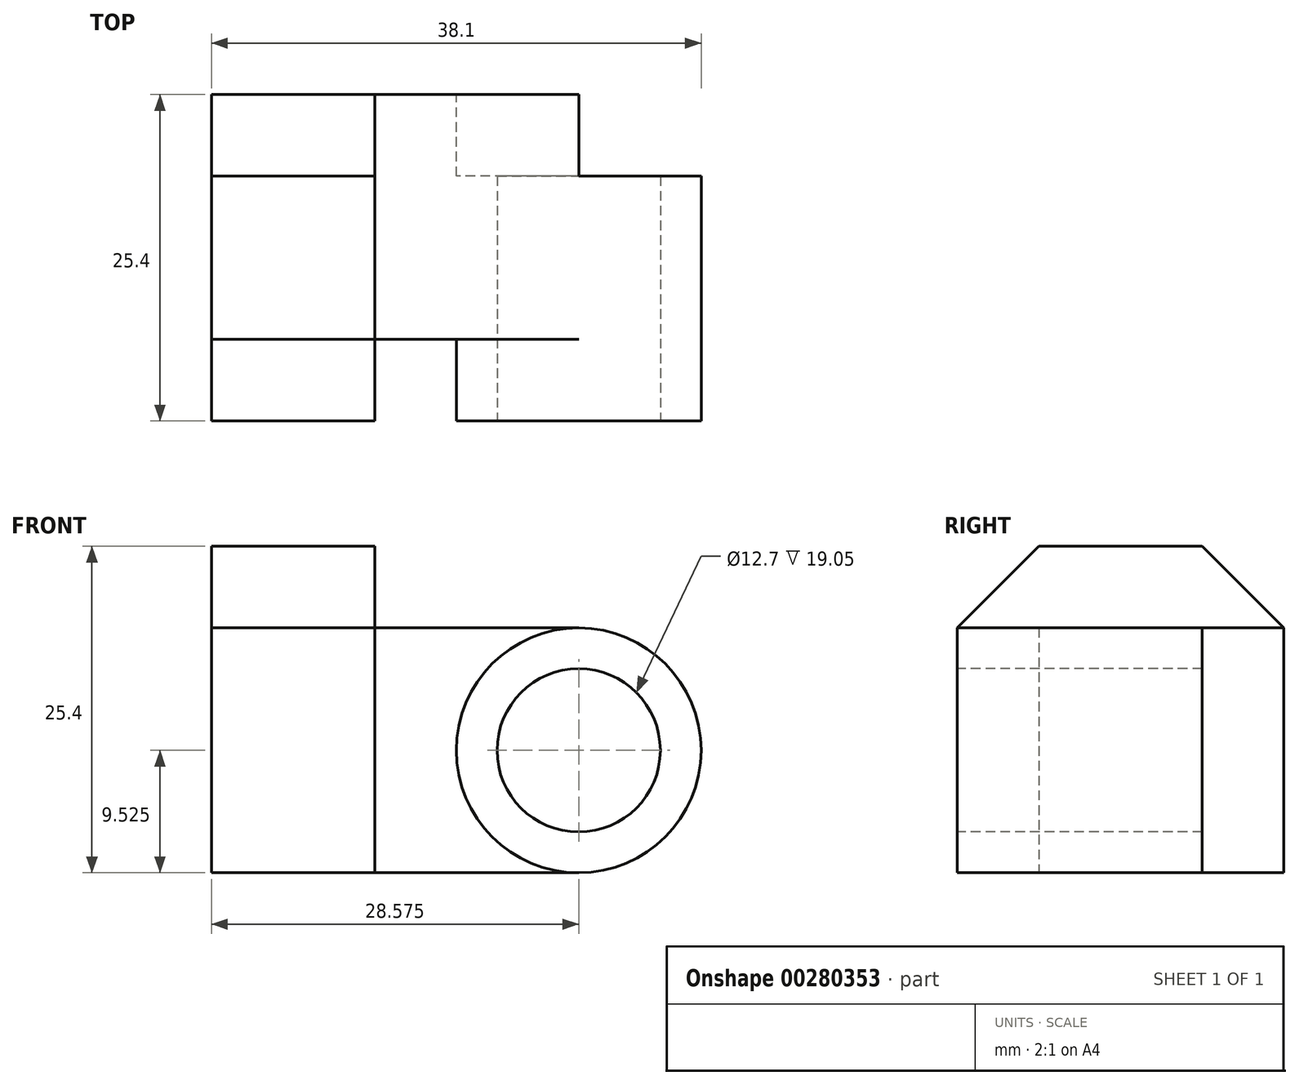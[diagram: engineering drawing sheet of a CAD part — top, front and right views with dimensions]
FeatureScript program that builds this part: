
annotation { "Feature Type Name" : "Feature", "Feature Type Description" : "" }
export const myFeature = defineFeature(function(context is Context, id is Id, definition is map)
    precondition{}
    {
        {
            var Q0;
            Q0=qCreatedBy(makeId("Top.planeOp"),FACE);
            var sketch = newSketch(context, id + "F0", { "sketchPlane" : qUnion([Q0])});
            skLineSegment(sketch, "E0.bottom", {"start": v(0, 0) * mm, "end": v(38.1, 0) * mm});
            skLineSegment(sketch, "E0.top", {"start": v(0, 25.4) * mm, "end": v(38.1, 25.4) * mm});
            skLineSegment(sketch, "E0.left", {"start": v(0, 0) * mm, "end": v(0, 25.4) * mm});
            skLineSegment(sketch, "E0.right", {"start": v(38.1, 0) * mm, "end": v(38.1, 25.4) * mm});
            skSolve(sketch);
        }
        {
            var Q0;
            Q0 = qSketchRegion(id + "F0", true);
            extrude(context, id + "F1", {"entities" : qUnion([Q0]), "depth" : 25.4 * mm});
        }
        {
            var Q0;
            Q0=makeQuery(id+"F1.opExtrude","SWEPT_FACE",FACE,{"disambiguationData":[OSD([sQuery(id+"F0.wireOp",EDGE,"E0.left")])]});
            var sketch = newSketch(context, id + "F2", { "sketchPlane" : qUnion([Q0])});
            skLineSegment(sketch, "E1", {"start": v(-25.4, 25.4) * mm, "end": v(-25.4, 19.05) * mm});
            skLineSegment(sketch, "E2", {"start": v(-25.4, 25.4) * mm, "end": v(-19.05, 25.4) * mm});
            skLineSegment(sketch, "E3", {"start": v(-19.05, 25.4) * mm, "end": v(-25.4, 19.05) * mm});
            skLineSegment(sketch, "E4", {"start": v(0, 25.4) * mm, "end": v(0, 19.05) * mm});
            skLineSegment(sketch, "E5", {"start": v(0, 25.4) * mm, "end": v(-6.35, 25.4) * mm});
            skLineSegment(sketch, "E6", {"start": v(-6.35, 25.4) * mm, "end": v(0, 19.05) * mm});
            skSolve(sketch);
        }
        {
            var Q0;
            Q0 = qSketchRegion(id + "F2", true);
            extrude(context, id + "F3", {"entities" : qUnion([Q0]), "operationType" : NewBodyOperationType.REMOVE, "oppositeDirection" : true, "depth" : 12.7 * mm});
        }
        {
            var Q0;
            Q0=makeQuery(id+"F1.opExtrude","SWEPT_FACE",FACE,{"disambiguationData":[OSD([sQuery(id+"F0.wireOp",EDGE,"E0.bottom")])]});
            var sketch = newSketch(context, id + "F4", { "sketchPlane" : qUnion([Q0])});
            skCircle(sketch, "E7", {"center": v(28.58, 9.53) * mm, "radius": 6.35 * mm});
            skCircle(sketch, "E8", {"center": v(28.58, 9.53) * mm, "radius": 9.53 * mm});
            skLineSegment(sketch, "E9", {"start": v(12.7, 19.05) * mm, "end": v(28.58, 19.05) * mm});
            skLineSegment(sketch, "E10", {"start": v(12.7, 19.05) * mm, "end": v(12.7, 0) * mm});
            skSolve(sketch);
        }
        {
            var Q0;
            {var subQ2=sQuery(id+"F4.wireOp",EDGE,"E9");Q0=makeQuery(id+"F4.imprint","IMPRINT",FACE,{"disambiguationData":[TD([[makeQuery(id+"F4.imprint","IMPRINT",EDGE,{"derivedFrom":subQ2}),1.0]])]});}
            var Q1;
            {var subQ0=sQuery(id+"F4.wireOp",EDGE,"E8");var subQ1=sQuery(id+"F0.wireOp",EDGE,"E0.bottom");var subQ4=makeQuery(id+"F1.opExtrude","CAP_EDGE",EDGE,{"disambiguationData":[OSD([subQ1])],"isStart":true});var subQ5=makeQuery(id+"F4.imprint","INTERSECT",VERTEX,{"derivedFrom":[subQ4,subQ0]});Q1=makeQuery(id+"F4.imprint","IMPRINT",FACE,{"disambiguationData":[TD([[makeQuery(id+"F4.imprint","IMPRINT",EDGE,{"disambiguationData":[TD([[subQ5,-1.0]])],"derivedFrom":subQ0}),-1.0]])]});}
            extrude(context, id + "F5", {"entities" : qUnion([Q0, Q1]), "operationType" : NewBodyOperationType.REMOVE, "oppositeDirection" : true, "depth" : 25.4 * mm});
        }
        {
            var Q0;
            {var subQ0=sQuery(id+"F4.wireOp",EDGE,"E9");Q0=makeQuery(id+"F4.imprint","IMPRINT",FACE,{"disambiguationData":[TD([[makeQuery(id+"F4.imprint","IMPRINT",EDGE,{"derivedFrom":subQ0}),-1.0]])]});}
            extrude(context, id + "F6", {"entities" : qUnion([Q0]), "operationType" : NewBodyOperationType.REMOVE, "oppositeDirection" : true, "depth" : 6.35 * mm});
        }
        {
            var Q0;
            Q0=makeQuery(id+"F4.imprint","IMPRINT",FACE,{"disambiguationData":[TD([[makeQuery(id+"F4.imprint","IMPRINT",EDGE,{"derivedFrom":sQuery(id+"F4.wireOp",EDGE,"E7")}),1.0]])]});
            extrude(context, id + "F7", {"entities" : qUnion([Q0]), "operationType" : NewBodyOperationType.REMOVE, "oppositeDirection" : true, "depth" : 25.4 * mm});
        }
        {
            var Q0;
            Q0=makeQuery(id+"F1.opExtrude","SWEPT_FACE",FACE,{"disambiguationData":[OSD([sQuery(id+"F0.wireOp",EDGE,"E0.top")])]});
            var sketch = newSketch(context, id + "F8", { "sketchPlane" : qUnion([Q0])});
            skCircle(sketch, "E11", {"center": v(-28.58, 9.53) * mm, "radius": 9.53 * mm});
            skLineSegment(sketch, "E12", {"start": v(-28.58, 19.05) * mm, "end": v(-12.7, 19.05) * mm});
            skLineSegment(sketch, "E13", {"start": v(-12.7, 19.05) * mm, "end": v(-12.7, 0) * mm});
            skLineSegment(sketch, "E14", {"start": v(-12.7, 0) * mm, "end": v(-28.58, 0) * mm});
            skSolve(sketch);
        }
        {
            var Q0;
            Q0=makeQuery(id+"F8.imprint","IMPRINT",FACE,{"disambiguationData":[TD([[makeQuery(id+"F8.imprint","IMPRINT",EDGE,{"disambiguationData":[OD(0.0)],"derivedFrom":sQuery(id+"F8.wireOp",EDGE,"E11")}),-1.0]])]});
            extrude(context, id + "F9", {"entities" : qUnion([Q0]), "operationType" : NewBodyOperationType.REMOVE, "oppositeDirection" : true, "depth" : 6.35 * mm});
        }
    });
